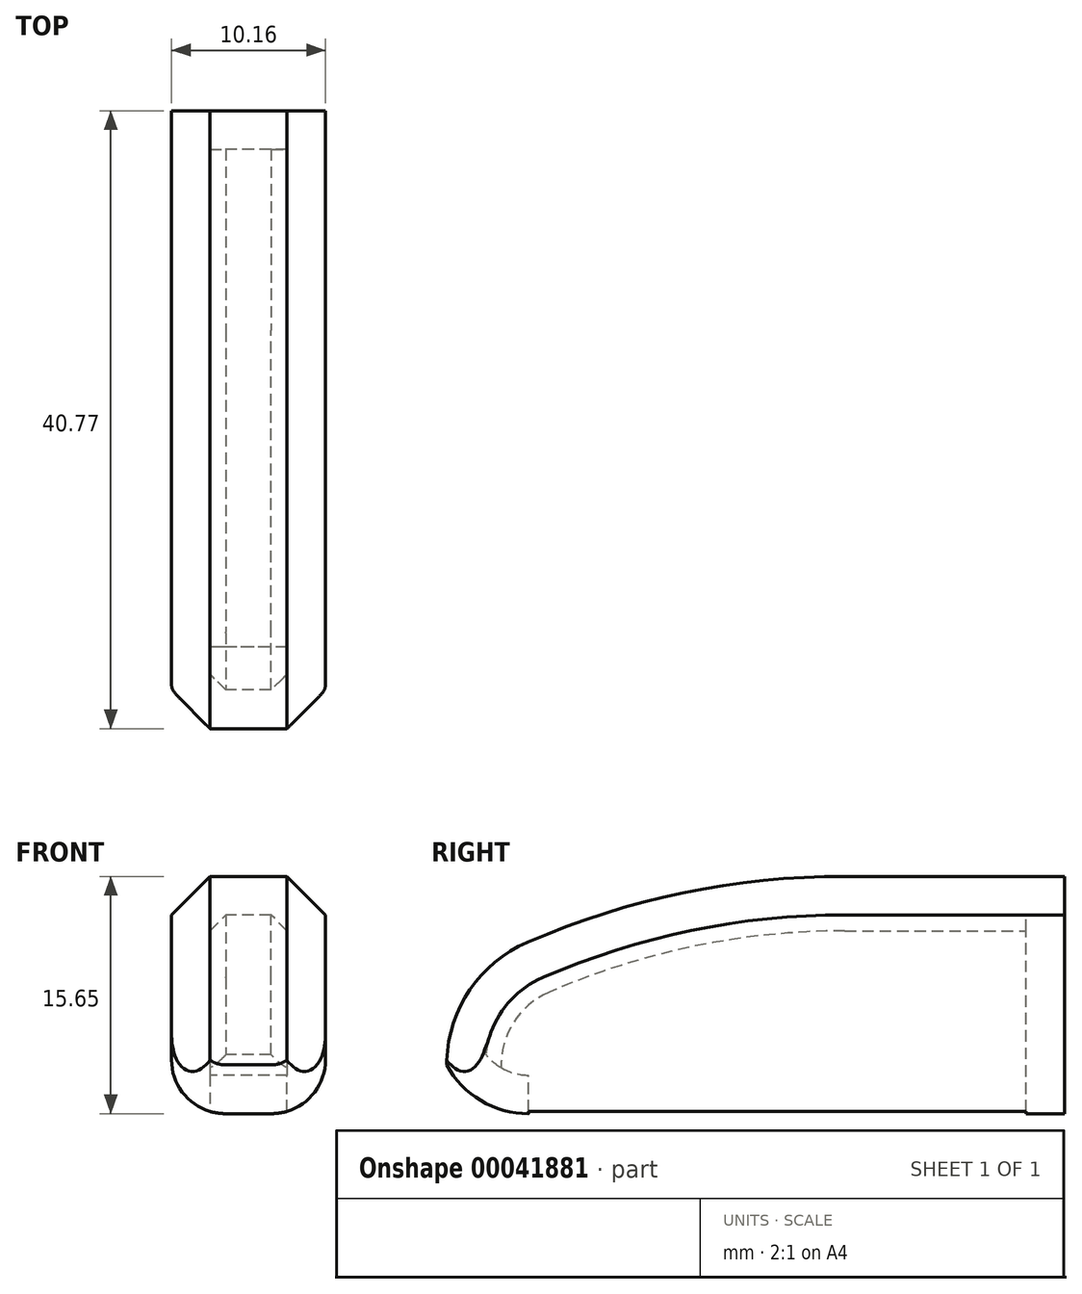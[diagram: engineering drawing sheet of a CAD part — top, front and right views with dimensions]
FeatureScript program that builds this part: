
annotation { "Feature Type Name" : "Feature", "Feature Type Description" : "" }
export const myFeature = defineFeature(function(context is Context, id is Id, definition is map)
    precondition{}
    {
        {
            var Q0;
            Q0=qCreatedBy(makeId("Right.planeOp"),FACE);
            var sketch = newSketch(context, id + "F0", { "sketchPlane" : qUnion([Q0])});
            skLineSegment(sketch, "E0.bottom", {"start": v(0, 0) * mm, "end": v(25.4, 0) * mm});
            skLineSegment(sketch, "E0.top", {"start": v(0, 15.65) * mm, "end": v(25.4, 15.65) * mm});
            skLineSegment(sketch, "E0.right", {"start": v(25.4, 0) * mm, "end": v(25.4, 15.65) * mm});
            skLineSegment(sketch, "E1", {"start": v(0, 15.65) * mm, "end": v(-15.37, 9) * mm});
            skLineSegment(sketch, "E2", {"start": v(-15.37, 9) * mm, "end": v(-15.37, 0) * mm});
            skLineSegment(sketch, "E3", {"start": v(-15.37, 0) * mm, "end": v(0, 0) * mm});
            skSolve(sketch);
        }
        {
            var Q0;
            Q0=makeQuery(id+"F0.imprint","IMPRINT",FACE,{"disambiguationData":[TD([[makeQuery(id+"F0.imprint","IMPRINT",EDGE,{"derivedFrom":sQuery(id+"F0.wireOp",EDGE,"E0.bottom")}),1.0]])]});
            extrude(context, id + "F1", {"entities" : qUnion([Q0]), "depth" : 10.16 * mm});
        }
        {
            var Q0;
            Q0=makeQuery(id+"F1.opExtrude","SWEPT_EDGE",EDGE,{"disambiguationData":[OSD([sQuery(id+"F0.wireOp",EDGE,"E1"),sQuery(id+"F0.wireOp",EDGE,"E2")])]});
            fillet(context, id + "F2", {"entities" : qUnion([Q0]), "radius" : 8.8 * mm, "tangentPropagation" : true, "allowEdgeOverflow" : false});
        }
        {
            var Q0;
            Q0=makeQuery(id+"F1.opExtrude","SWEPT_EDGE",EDGE,{"disambiguationData":[OSD([sQuery(id+"F0.wireOp",EDGE,"E2"),sQuery(id+"F0.wireOp",EDGE,"E3")])]});
            fillet(context, id + "F3", {"entities" : qUnion([Q0]), "radius" : 6.15 * mm, "tangentPropagation" : true, "allowEdgeOverflow" : false});
        }
        {
            var Q0;
            Q0=makeQuery(id+"F1.opExtrude","SWEPT_EDGE",EDGE,{"disambiguationData":[OSD([sQuery(id+"F0.wireOp",EDGE,"E0.top"),sQuery(id+"F0.wireOp",EDGE,"E1")])]});
            fillet(context, id + "F4", {"entities" : qUnion([Q0]), "radius" : 52.58 * mm, "tangentPropagation" : true, "allowEdgeOverflow" : false});
        }
        {
            var Q0;
            {var subQ0=sQuery(id+"F0.wireOp",EDGE,"E1");var subQ1=sQuery(id+"F0.wireOp",EDGE,"E2");Q0=makeQuery(id+"F2.opFillet","BLEND_EDGE",EDGE,{"blendedFrom":[makeQuery(id+"F1.opExtrude","SWEPT_EDGE",EDGE,{"disambiguationData":[OSD([subQ0,subQ1])]}),makeQuery(id+"F1.opExtrude","CAP_FACE",FACE,{"disambiguationData":[OSD([sQuery(id+"F0.wireOp",EDGE,"E0.bottom"),sQuery(id+"F0.wireOp",EDGE,"E0.top"),sQuery(id+"F0.wireOp",EDGE,"E0.right"),subQ0,subQ1,sQuery(id+"F0.wireOp",EDGE,"E3")])],"isStart":true})],"blendedInto":[makeQuery(id+"F1.opExtrude","CAP_FACE",FACE,{"disambiguationData":[OSD([sQuery(id+"F0.wireOp",EDGE,"E0.bottom"),sQuery(id+"F0.wireOp",EDGE,"E0.top"),sQuery(id+"F0.wireOp",EDGE,"E0.right"),subQ0,subQ1,sQuery(id+"F0.wireOp",EDGE,"E3")])],"isStart":true})]});}
            var Q1;
            {var subQ0=sQuery(id+"F0.wireOp",EDGE,"E0.top");var subQ1=sQuery(id+"F0.wireOp",EDGE,"E1");Q1=makeQuery(id+"F4.opFillet","BLEND_EDGE",EDGE,{"blendedFrom":[makeQuery(id+"F1.opExtrude","SWEPT_EDGE",EDGE,{"disambiguationData":[OSD([subQ0,subQ1])]}),makeQuery(id+"F1.opExtrude","CAP_FACE",FACE,{"disambiguationData":[OSD([sQuery(id+"F0.wireOp",EDGE,"E0.bottom"),subQ0,sQuery(id+"F0.wireOp",EDGE,"E0.right"),subQ1,sQuery(id+"F0.wireOp",EDGE,"E2"),sQuery(id+"F0.wireOp",EDGE,"E3")])],"isStart":false})],"blendedInto":[makeQuery(id+"F1.opExtrude","CAP_FACE",FACE,{"disambiguationData":[OSD([sQuery(id+"F0.wireOp",EDGE,"E0.bottom"),subQ0,sQuery(id+"F0.wireOp",EDGE,"E0.right"),subQ1,sQuery(id+"F0.wireOp",EDGE,"E2"),sQuery(id+"F0.wireOp",EDGE,"E3")])],"isStart":false})]});}
            chamfer(context, id + "F5", {"entities" : qUnion([Q0, Q1]), "width" : 2.54 * mm, "tangentPropagation" : true});
        }
        {
            var Q0;
            Q0=makeQuery(id+"F1.opExtrude","SWEPT_FACE",FACE,{"disambiguationData":[OSD([sQuery(id+"F0.wireOp",EDGE,"E0.bottom"),sQuery(id+"F0.wireOp",EDGE,"E3")])]});
            shell(context, id + "F6", {"entities" : qUnion([Q0]), "thickness" : 2.54 * mm});
        }
        {
            var Q0;
            Q0=makeQuery(id+"F1.opExtrude","CAP_EDGE",EDGE,{"disambiguationData":[OSD([sQuery(id+"F0.wireOp",EDGE,"E0.bottom"),sQuery(id+"F0.wireOp",EDGE,"E3")])],"isStart":true});
            var Q1;
            Q1=makeQuery(id+"F1.opExtrude","CAP_EDGE",EDGE,{"disambiguationData":[OSD([sQuery(id+"F0.wireOp",EDGE,"E0.bottom"),sQuery(id+"F0.wireOp",EDGE,"E3")])],"isStart":false});
            fillet(context, id + "F7", {"entities" : qUnion([Q0, Q1]), "radius" : 3.56 * mm, "tangentPropagation" : true, "allowEdgeOverflow" : false});
        }
    });
